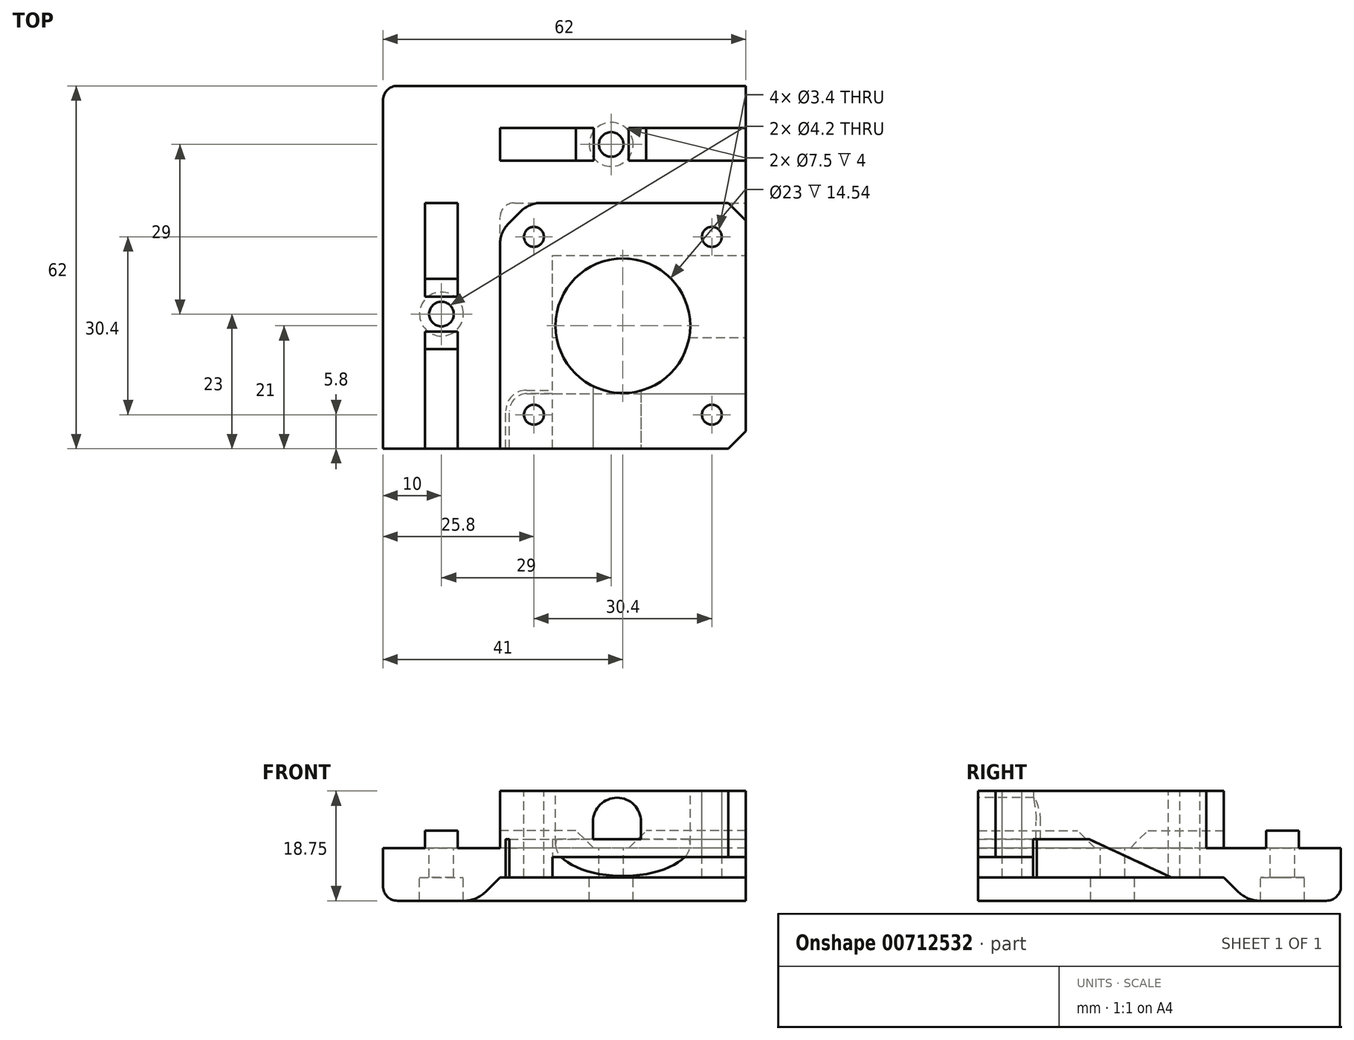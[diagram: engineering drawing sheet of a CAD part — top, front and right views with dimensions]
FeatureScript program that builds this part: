
annotation { "Feature Type Name" : "Feature", "Feature Type Description" : "" }
export const myFeature = defineFeature(function(context is Context, id is Id, definition is map)
    precondition{}
    {
        {
            var Q0;
            Q0=qCreatedBy(makeId("Top.planeOp"),FACE);
            var sketch = newSketch(context, id + "F0", { "sketchPlane" : qUnion([Q0])});
            skLineSegment(sketch, "E0.bottom", {"start": v(0, 0) * mm, "end": v(59, 0) * mm});
            skLineSegment(sketch, "E0.top", {"start": v(0, 54) * mm, "end": v(59, 54) * mm});
            skLineSegment(sketch, "E0.left", {"start": v(0, 0) * mm, "end": v(0, 54) * mm});
            skLineSegment(sketch, "E0.right", {"start": v(59, 0) * mm, "end": v(59, 54) * mm});
            skSolve(sketch);
        }
        {
            var Q0;
            Q0=makeQuery(id+"F0.imprint","IMPRINT",FACE,{"disambiguationData":[TD([[makeQuery(id+"F0.imprint","IMPRINT",EDGE,{"derivedFrom":sQuery(id+"F0.wireOp",EDGE,"E0.bottom")}),1.0]])]});
            extrude(context, id + "F1", {"entities" : qUnion([Q0]), "depth" : 5 * mm, "offsetDistance" : 25 * mm});
        }
        {
            var Q0;
            Q0=makeQuery(id+"F1.opExtrude","CAP_FACE",FACE,{"disambiguationData":[OSD([sQuery(id+"F0.wireOp",EDGE,"E0.bottom"),sQuery(id+"F0.wireOp",EDGE,"E0.top"),sQuery(id+"F0.wireOp",EDGE,"E0.left"),sQuery(id+"F0.wireOp",EDGE,"E0.right")])],"isStart":false});
            var sketch = newSketch(context, id + "F2", { "sketchPlane" : qUnion([Q0])});
            skLineSegment(sketch, "E1.bottom", {"start": v(59, 0) * mm, "end": v(17, 0) * mm});
            skLineSegment(sketch, "E1.top", {"start": v(59, 42) * mm, "end": v(17, 42) * mm});
            skLineSegment(sketch, "E1.left", {"start": v(59, 0) * mm, "end": v(59, 42) * mm});
            skLineSegment(sketch, "E1.right", {"start": v(17, 0) * mm, "end": v(17, 42) * mm});
            skSolve(sketch);
        }
        {
            var Q0;
            Q0=makeQuery(id+"F2.imprint","IMPRINT",FACE,{"disambiguationData":[TD([[makeQuery(id+"F2.imprint","IMPRINT",EDGE,{"derivedFrom":sQuery(id+"F2.wireOp",EDGE,"E1.bottom")}),1.0]])]});
            extrude(context, id + "F3", {"entities" : qUnion([Q0]), "operationType" : NewBodyOperationType.ADD, "depth" : 9.75 * mm, "offsetDistance" : 25 * mm});
        }
        {
            var Q0;
            Q0=makeQuery(id+"F3.boolean.opBoolean","MERGE",FACE,{"derivedFrom":[makeQuery(id+"F1.opExtrude","SWEPT_FACE",FACE,{"disambiguationData":[OSD([sQuery(id+"F0.wireOp",EDGE,"E0.right")])]}),makeQuery(id+"F3.opExtrude","SWEPT_FACE",FACE,{"disambiguationData":[OSD([sQuery(id+"F2.wireOp",EDGE,"E1.left")])]})]});
            var sketch = newSketch(context, id + "F4", { "sketchPlane" : qUnion([Q0])});
            skLineSegment(sketch, "E2", {"start": v(0, 0) * mm, "end": v(0, 6.5) * mm});
            skLineSegment(sketch, "E3", {"start": v(0, 6.5) * mm, "end": v(19, 6.5) * mm});
            skLineSegment(sketch, "E4", {"start": v(19, 6.5) * mm, "end": v(33, 0) * mm});
            skLineSegment(sketch, "E5", {"start": v(33, 0) * mm, "end": v(0, 0) * mm});
            skSolve(sketch);
        }
        {
            var Q0;
            Q0=makeQuery(id+"F4.imprint","IMPRINT",FACE,{"disambiguationData":[TD([[makeQuery(id+"F4.imprint","IMPRINT",EDGE,{"derivedFrom":sQuery(id+"F4.wireOp",EDGE,"E2")}),1.0]])]});
            extrude(context, id + "F5", {"entities" : qUnion([Q0]), "operationType" : NewBodyOperationType.REMOVE, "oppositeDirection" : true, "depth" : 33 * mm, "offsetDistance" : 25 * mm});
        }
        {
            var Q0;
            Q0=makeQuery(id+"F3.opExtrude","CAP_FACE",FACE,{"disambiguationData":[OSD([sQuery(id+"F2.wireOp",EDGE,"E1.bottom"),sQuery(id+"F2.wireOp",EDGE,"E1.top"),sQuery(id+"F2.wireOp",EDGE,"E1.left"),sQuery(id+"F2.wireOp",EDGE,"E1.right")])],"isStart":false});
            var sketch = newSketch(context, id + "F6", { "sketchPlane" : qUnion([Q0])});
            skCircle(sketch, "E6", {"center": v(38, 21) * mm, "radius": 11.5 * mm});
            skCircle(sketch, "E7", {"center": v(22.8, 36.2) * mm, "radius": 1.7 * mm});
            skCircle(sketch, "E8", {"center": v(53.2, 36.2) * mm, "radius": 1.7 * mm});
            skCircle(sketch, "E9", {"center": v(22.8, 5.8) * mm, "radius": 1.7 * mm});
            skCircle(sketch, "E10", {"center": v(53.2, 5.8) * mm, "radius": 1.7 * mm});
            skSolve(sketch);
        }
        {
            var Q0;
            Q0=makeQuery(id+"F6.imprint","IMPRINT",FACE,{"disambiguationData":[TD([[makeQuery(id+"F6.imprint","IMPRINT",EDGE,{"derivedFrom":sQuery(id+"F6.wireOp",EDGE,"E7")}),1.0]])]});
            var Q1;
            Q1=makeQuery(id+"F6.imprint","IMPRINT",FACE,{"disambiguationData":[TD([[makeQuery(id+"F6.imprint","IMPRINT",EDGE,{"derivedFrom":sQuery(id+"F6.wireOp",EDGE,"E6")}),1.0]])]});
            var Q2;
            Q2=makeQuery(id+"F6.imprint","IMPRINT",FACE,{"disambiguationData":[TD([[makeQuery(id+"F6.imprint","IMPRINT",EDGE,{"derivedFrom":sQuery(id+"F6.wireOp",EDGE,"E8")}),1.0]])]});
            var Q3;
            Q3=makeQuery(id+"F6.imprint","IMPRINT",FACE,{"disambiguationData":[TD([[makeQuery(id+"F6.imprint","IMPRINT",EDGE,{"derivedFrom":sQuery(id+"F6.wireOp",EDGE,"E9")}),1.0]])]});
            var Q4;
            Q4=makeQuery(id+"F6.imprint","IMPRINT",FACE,{"disambiguationData":[TD([[makeQuery(id+"F6.imprint","IMPRINT",EDGE,{"derivedFrom":sQuery(id+"F6.wireOp",EDGE,"E10")}),1.0]])]});
            var Q5;
            Q5=makeQuery(id+"F6.imprint","IMPRINT",FACE,{"disambiguationData":[TD([[makeQuery(id+"F6.imprint","IMPRINT",EDGE,{"derivedFrom":sQuery(id+"F6.wireOp",EDGE,"STXgVHVY-l6Oo-r3We-HZuw-ze8qtC1o8g8W")}),1.0]])]});
            extrude(context, id + "F7", {"entities" : qUnion([Q0, Q1, Q2, Q3, Q4, Q5]), "operationType" : NewBodyOperationType.REMOVE, "endBound" : BoundingType.THROUGH_ALL, "oppositeDirection" : true, "depth" : 25 * mm, "offsetDistance" : 25 * mm});
        }
        {
            var Q0;
            Q0=makeQuery(id+"F3.opExtrude","SWEPT_EDGE",EDGE,{"disambiguationData":[OSD([sQuery(id+"F0.wireOp",EDGE,"E0.right"),sQuery(id+"F2.wireOp",EDGE,"E1.top"),sQuery(id+"F2.wireOp",EDGE,"E1.left")])]});
            var Q1;
            Q1=makeQuery(id+"F3.boolean.opBoolean","MERGE",EDGE,{"derivedFrom":[makeQuery(id+"F1.opExtrude","SWEPT_EDGE",EDGE,{"disambiguationData":[OSD([sQuery(id+"F0.wireOp",EDGE,"E0.bottom"),sQuery(id+"F0.wireOp",EDGE,"E0.right")])]}),makeQuery(id+"F3.opExtrude","SWEPT_EDGE",EDGE,{"disambiguationData":[OSD([sQuery(id+"F2.wireOp",EDGE,"E1.bottom"),sQuery(id+"F2.wireOp",EDGE,"E1.left")])]})]});
            chamfer(context, id + "F8", {"entities" : qUnion([Q0, Q1]), "width" : 3 * mm, "tangentPropagation" : true});
        }
        {
            var Q0;
            Q0=makeQuery(id+"F3.boolean.opBoolean","MERGE",FACE,{"derivedFrom":[makeQuery(id+"F7aVUtGTQ7vZGl7_1.boolean.opBoolean","MERGE",FACE,{"derivedFrom":[makeQuery(id+"F1.opExtrude","SWEPT_FACE",FACE,{"disambiguationData":[OSD([sQuery(id+"F0.wireOp",EDGE,"E0.bottom")])]}),makeQuery(id+"F7aVUtGTQ7vZGl7_1.opExtrude","SWEPT_FACE",FACE,{"disambiguationData":[OSD([sQuery(id+"Fs2P3l27It3FXby_1.wireOp",EDGE,"bHcCaI8n-BMMI-Yc99-4eW4-bQ5ukSnPJtkv.top")])]})]}),makeQuery(id+"F3.opExtrude","SWEPT_FACE",FACE,{"disambiguationData":[OSD([sQuery(id+"F2.wireOp",EDGE,"E1.bottom")])]})]});
            var sketch = newSketch(context, id + "F9", { "sketchPlane" : qUnion([Q0])});
            skLineSegment(sketch, "E11.top", {"start": v(32.9, 6.5) * mm, "end": v(41.1, 6.5) * mm});
            skLineSegment(sketch, "E11.left", {"start": v(32.9, 9.5) * mm, "end": v(32.9, 6.5) * mm});
            skLineSegment(sketch, "E11.right", {"start": v(41.1, 9.5) * mm, "end": v(41.1, 6.5) * mm});
            skArc(sketch, "E12.trimOffspring", {"start": v(41.1, 9.5) * mm, "mid": v(37, 13.6) * mm, "end": v(32.9, 9.5) * mm});
            skSolve(sketch);
        }
        {
            var Q0;
            Q0=makeQuery(id+"F9.imprint","IMPRINT",FACE,{"disambiguationData":[TD([[makeQuery(id+"F9.imprint","IMPRINT",EDGE,{"derivedFrom":sQuery(id+"F9.wireOp",EDGE,"E11.top")}),1.0]])]});
            extrude(context, id + "F10", {"entities" : qUnion([Q0]), "operationType" : NewBodyOperationType.REMOVE, "endBound" : BoundingType.UP_TO_NEXT, "oppositeDirection" : true, "depth" : 25 * mm, "offsetDistance" : 25 * mm});
        }
        {
            var Q0;
            Q0=makeQuery(id+"F1.opExtrude","CAP_FACE",FACE,{"disambiguationData":[OSD([sQuery(id+"F0.wireOp",EDGE,"E0.bottom"),sQuery(id+"F0.wireOp",EDGE,"E0.top"),sQuery(id+"F0.wireOp",EDGE,"E0.left"),sQuery(id+"F0.wireOp",EDGE,"E0.right")])],"isStart":false});
            var sketch = newSketch(context, id + "F11", { "sketchPlane" : qUnion([Q0])});
            skLineSegment(sketch, "E13", {"start": v(56, 42) * mm, "end": v(59, 42) * mm});
            skSolve(sketch);
        }
        {
            var Q0;
            {var subQ1=sQuery(id+"F11.wireOp",EDGE,"E13");Q0=makeQuery(id+"F11.imprint","IMPRINT",FACE,{"disambiguationData":[TD([[makeQuery(id+"F11.imprint","IMPRINT",EDGE,{"derivedFrom":subQ1}),1.0]])]});}
            extrude(context, id + "F12", {"entities" : qUnion([Q0]), "operationType" : NewBodyOperationType.REMOVE, "endBound" : BoundingType.THROUGH_ALL, "oppositeDirection" : true, "depth" : 25 * mm, "offsetDistance" : 25 * mm});
        }
        {
            var Q0;
            {var subQ0=sQuery(id+"F2.wireOp",EDGE,"E1.top");Q0=makeQuery(id+"F12.boolean.opBoolean","MERGE",FACE,{"derivedFrom":[makeQuery(id+"F3.opExtrude","SWEPT_FACE",FACE,{"disambiguationData":[OSD([subQ0])]})],"fromTools":[makeQuery(id+"F12.opExtrude","SWEPT_FACE",FACE,{"disambiguationData":[OSD([subQ0,sQuery(id+"F11.wireOp",EDGE,"E13")])]})]});}
            var sketch = newSketch(context, id + "F13", { "sketchPlane" : qUnion([Q0])});
            skLineSegment(sketch, "E14.bottom", {"start": v(-59, 5) * mm, "end": v(-17, 5) * mm});
            skLineSegment(sketch, "E14.top", {"start": v(-59, 0) * mm, "end": v(-17, 0) * mm});
            skLineSegment(sketch, "E14.left", {"start": v(-59, 5) * mm, "end": v(-59, 0) * mm});
            skLineSegment(sketch, "E14.right", {"start": v(-17, 5) * mm, "end": v(-17, 0) * mm});
            skSolve(sketch);
        }
        {
            var Q0;
            Q0=makeQuery(id+"F13.imprint","IMPRINT",FACE,{"disambiguationData":[TD([[makeQuery(id+"F13.imprint","IMPRINT",EDGE,{"derivedFrom":sQuery(id+"F13.wireOp",EDGE,"E14.top")}),1.0]])]});
            extrude(context, id + "F14", {"entities" : qUnion([Q0]), "operationType" : NewBodyOperationType.ADD, "depth" : 20 * mm, "offsetDistance" : 25 * mm});
        }
        {
            var Q0;
            {var subQ0=sQuery(id+"F2.wireOp",EDGE,"E1.right");Q0=makeQuery(id+"F14.boolean.opBoolean","MERGE",FACE,{"derivedFrom":[makeQuery(id+"F12.boolean.opBoolean","MERGE",FACE,{"derivedFrom":[makeQuery(id+"F3.opExtrude","SWEPT_FACE",FACE,{"disambiguationData":[OSD([subQ0])]})],"fromTools":[makeQuery(id+"F12.opExtrude","SWEPT_FACE",FACE,{"disambiguationData":[OSD([subQ0])]})]}),makeQuery(id+"F14.opExtrude","SWEPT_FACE",FACE,{"disambiguationData":[OSD([sQuery(id+"F13.wireOp",EDGE,"E14.right")])]})]});}
            var sketch = newSketch(context, id + "F15", { "sketchPlane" : qUnion([Q0])});
            skLineSegment(sketch, "E15.bottom", {"start": v(-62, 5) * mm, "end": v(0, 5) * mm});
            skLineSegment(sketch, "E15.top", {"start": v(-62, 0) * mm, "end": v(0, 0) * mm});
            skLineSegment(sketch, "E15.left", {"start": v(-62, 5) * mm, "end": v(-62, 0) * mm});
            skLineSegment(sketch, "E15.right", {"start": v(0, 5) * mm, "end": v(0, 0) * mm});
            skSolve(sketch);
        }
        {
            var Q0;
            Q0=makeQuery(id+"F15.imprint","IMPRINT",FACE,{"disambiguationData":[TD([[makeQuery(id+"F15.imprint","IMPRINT",EDGE,{"derivedFrom":sQuery(id+"F15.wireOp",EDGE,"E15.top")}),-1.0]])]});
            extrude(context, id + "F16", {"entities" : qUnion([Q0]), "operationType" : NewBodyOperationType.ADD, "depth" : 20 * mm, "offsetDistance" : 25 * mm});
        }
        {
            var Q0;
            Q0=makeQuery(id+"F16.boolean.opBoolean","MERGE",FACE,{"derivedFrom":[makeQuery(id+"F14.boolean.opBoolean","MERGE",FACE,{"derivedFrom":[makeQuery(id+"F1.opExtrude","CAP_FACE",FACE,{"disambiguationData":[OSD([sQuery(id+"F0.wireOp",EDGE,"E0.bottom"),sQuery(id+"F0.wireOp",EDGE,"E0.top"),sQuery(id+"F0.wireOp",EDGE,"E0.left"),sQuery(id+"F0.wireOp",EDGE,"E0.right")])],"isStart":false}),makeQuery(id+"F14.opExtrude","SWEPT_FACE",FACE,{"disambiguationData":[OSD([sQuery(id+"F13.wireOp",EDGE,"E14.bottom")])]})]}),makeQuery(id+"F16.opExtrude","SWEPT_FACE",FACE,{"disambiguationData":[OSD([sQuery(id+"F15.wireOp",EDGE,"E15.bottom")])]})]});
            var sketch = newSketch(context, id + "F17", { "sketchPlane" : qUnion([Q0])});
            skLineSegment(sketch, "E16.bottom", {"start": v(59, 54.8) * mm, "end": v(17, 54.8) * mm});
            skLineSegment(sketch, "E16.top", {"start": v(59, 49.2) * mm, "end": v(17, 49.2) * mm});
            skLineSegment(sketch, "E16.left", {"start": v(59, 54.8) * mm, "end": v(59, 49.2) * mm});
            skLineSegment(sketch, "E16.right", {"start": v(17, 54.8) * mm, "end": v(17, 49.2) * mm});
            skLineSegment(sketch, "E17.bottom", {"start": v(4.2, 0) * mm, "end": v(9.8, 0) * mm});
            skLineSegment(sketch, "E17.top", {"start": v(4.2, 42) * mm, "end": v(9.8, 42) * mm});
            skLineSegment(sketch, "E17.left", {"start": v(4.2, 0) * mm, "end": v(4.2, 42) * mm});
            skLineSegment(sketch, "E17.right", {"start": v(9.8, 0) * mm, "end": v(9.8, 42) * mm});
            skLineSegment(sketch, "E18.bottom", {"start": v(22, 54.8) * mm, "end": v(28, 54.8) * mm});
            skLineSegment(sketch, "E19.bottom", {"start": v(33, 54.8) * mm, "end": v(39, 54.8) * mm});
            skLineSegment(sketch, "E19.top", {"start": v(33, 49.2) * mm, "end": v(39, 49.2) * mm});
            skLineSegment(sketch, "E19.left", {"start": v(33, 54.8) * mm, "end": v(33, 49.2) * mm});
            skLineSegment(sketch, "E19.right", {"start": v(39, 54.8) * mm, "end": v(39, 49.2) * mm});
            skLineSegment(sketch, "E20.left", {"start": v(4.2, 37) * mm, "end": v(4.2, 31) * mm});
            skLineSegment(sketch, "E20.right", {"start": v(9.8, 37) * mm, "end": v(9.8, 31) * mm});
            skLineSegment(sketch, "E21.bottom", {"start": v(4.2, 26) * mm, "end": v(9.8, 26) * mm});
            skLineSegment(sketch, "E21.top", {"start": v(4.2, 20) * mm, "end": v(9.8, 20) * mm});
            skLineSegment(sketch, "E21.left", {"start": v(4.2, 26) * mm, "end": v(4.2, 20) * mm});
            skLineSegment(sketch, "E21.right", {"start": v(9.8, 26) * mm, "end": v(9.8, 20) * mm});
            skSolve(sketch);
        }
        {
            var Q0;
            {var subQ0=sQuery(id+"F17.wireOp",EDGE,"E20.top");Q0=makeQuery(id+"F17.imprint","IMPRINT",FACE,{"disambiguationData":[TD([[makeQuery(id+"F17.imprint","IMPRINT",EDGE,{"derivedFrom":subQ0}),-1.0]])]});}
            var Q1;
            {var subQ0=sQuery(id+"F17.wireOp",EDGE,"E17.top");Q1=makeQuery(id+"F17.imprint","IMPRINT",FACE,{"disambiguationData":[TD([[makeQuery(id+"F17.imprint","IMPRINT",EDGE,{"derivedFrom":subQ0}),-1.0]])]});}
            var Q2;
            {var subQ0=sQuery(id+"F17.wireOp",EDGE,"E17.bottom");Q2=makeQuery(id+"F17.imprint","IMPRINT",FACE,{"disambiguationData":[TD([[makeQuery(id+"F17.imprint","IMPRINT",EDGE,{"derivedFrom":subQ0}),1.0]])]});}
            var Q3;
            {var subQ0=sQuery(id+"F17.wireOp",EDGE,"E16.right");Q3=makeQuery(id+"F17.imprint","IMPRINT",FACE,{"disambiguationData":[TD([[makeQuery(id+"F17.imprint","IMPRINT",EDGE,{"derivedFrom":subQ0}),1.0]])]});}
            var Q4;
            {var subQ0=sQuery(id+"F17.wireOp",EDGE,"E18.right");Q4=makeQuery(id+"F17.imprint","IMPRINT",FACE,{"disambiguationData":[TD([[makeQuery(id+"F17.imprint","IMPRINT",EDGE,{"derivedFrom":subQ0}),1.0]])]});}
            var Q5;
            {var subQ0=sQuery(id+"F17.wireOp",EDGE,"E16.left");Q5=makeQuery(id+"F17.imprint","IMPRINT",FACE,{"disambiguationData":[TD([[makeQuery(id+"F17.imprint","IMPRINT",EDGE,{"derivedFrom":subQ0}),1.0]])]});}
            extrude(context, id + "F18", {"entities" : qUnion([Q0, Q1, Q2, Q3, Q4, Q5]), "operationType" : NewBodyOperationType.ADD, "depth" : 3 * mm, "offsetDistance" : 25 * mm});
        }
        {
            var Q0;
            Q0=makeQuery(id+"F18.opExtrude","CAP_EDGE",EDGE,{"disambiguationData":[OSD([sQuery(id+"F17.wireOp",EDGE,"E19.right")])],"isStart":false});
            var Q1;
            Q1=makeQuery(id+"F18.opExtrude","CAP_EDGE",EDGE,{"disambiguationData":[OSD([sQuery(id+"F17.wireOp",EDGE,"E19.left")])],"isStart":false});
            var Q2;
            Q2=makeQuery(id+"F18.opExtrude","CAP_EDGE",EDGE,{"disambiguationData":[OSD([sQuery(id+"F17.wireOp",EDGE,"E18.right")])],"isStart":false});
            var Q3;
            Q3=makeQuery(id+"F18.opExtrude","CAP_EDGE",EDGE,{"disambiguationData":[OSD([sQuery(id+"F17.wireOp",EDGE,"E18.left")])],"isStart":false});
            var Q4;
            Q4=makeQuery(id+"F18.opExtrude","CAP_EDGE",EDGE,{"disambiguationData":[OSD([sQuery(id+"F17.wireOp",EDGE,"E20.bottom")])],"isStart":false});
            var Q5;
            Q5=makeQuery(id+"F18.opExtrude","CAP_EDGE",EDGE,{"disambiguationData":[OSD([sQuery(id+"F17.wireOp",EDGE,"E20.top")])],"isStart":false});
            var Q6;
            Q6=makeQuery(id+"F18.opExtrude","CAP_EDGE",EDGE,{"disambiguationData":[OSD([sQuery(id+"F17.wireOp",EDGE,"E21.bottom")])],"isStart":false});
            var Q7;
            Q7=makeQuery(id+"F18.opExtrude","CAP_EDGE",EDGE,{"disambiguationData":[OSD([sQuery(id+"F17.wireOp",EDGE,"E21.top")])],"isStart":false});
            chamfer(context, id + "F19", {"entities" : qUnion([Q0, Q1, Q2, Q3, Q4, Q5, Q6, Q7]), "width" : 3 * mm, "tangentPropagation" : true});
        }
        {
            var Q0;
            Q0=makeQuery(id+"F16.boolean.opBoolean","MERGE",FACE,{"derivedFrom":[makeQuery(id+"F14.boolean.opBoolean","MERGE",FACE,{"derivedFrom":[makeQuery(id+"F1.opExtrude","CAP_FACE",FACE,{"disambiguationData":[OSD([sQuery(id+"F0.wireOp",EDGE,"E0.bottom"),sQuery(id+"F0.wireOp",EDGE,"E0.top"),sQuery(id+"F0.wireOp",EDGE,"E0.left"),sQuery(id+"F0.wireOp",EDGE,"E0.right")])],"isStart":false}),makeQuery(id+"F14.opExtrude","SWEPT_FACE",FACE,{"disambiguationData":[OSD([sQuery(id+"F13.wireOp",EDGE,"E14.bottom")])]})]}),makeQuery(id+"F16.opExtrude","SWEPT_FACE",FACE,{"disambiguationData":[OSD([sQuery(id+"F15.wireOp",EDGE,"E15.bottom")])]})]});
            var sketch = newSketch(context, id + "F20", { "sketchPlane" : qUnion([Q0])});
            skCircle(sketch, "E22", {"center": v(36, 52) * mm, "radius": 2.1 * mm});
            skCircle(sketch, "E23", {"center": v(7, 23) * mm, "radius": 2.1 * mm});
            skPoint(sketch, "E23.centerSnap0", {"position": v(7, 20) * mm});
            skSolve(sketch);
        }
        {
            var Q0;
            Q0=makeQuery(id+"F20.imprint","IMPRINT",FACE,{"disambiguationData":[TD([[makeQuery(id+"F20.imprint","IMPRINT",EDGE,{"derivedFrom":sQuery(id+"F20.wireOp",EDGE,"3zCe3JNz-EdKe-6DJv-AUvG-g2xwXIvxGB8e")}),1.0]])]});
            var Q1;
            Q1=makeQuery(id+"F20.imprint","IMPRINT",FACE,{"disambiguationData":[TD([[makeQuery(id+"F20.imprint","IMPRINT",EDGE,{"derivedFrom":sQuery(id+"F20.wireOp",EDGE,"E23")}),1.0]])]});
            var Q2;
            Q2=makeQuery(id+"F20.imprint","IMPRINT",FACE,{"disambiguationData":[TD([[makeQuery(id+"F20.imprint","IMPRINT",EDGE,{"derivedFrom":sQuery(id+"F20.wireOp",EDGE,"QEAMcVXS-o3zG-8i1c-1XAg-jgGJsIAo5R6x")}),1.0]])]});
            var Q3;
            Q3=makeQuery(id+"F20.imprint","IMPRINT",FACE,{"disambiguationData":[TD([[makeQuery(id+"F20.imprint","IMPRINT",EDGE,{"derivedFrom":sQuery(id+"F20.wireOp",EDGE,"E22")}),1.0]])]});
            extrude(context, id + "F21", {"entities" : qUnion([Q0, Q1, Q2, Q3]), "operationType" : NewBodyOperationType.REMOVE, "endBound" : BoundingType.THROUGH_ALL, "oppositeDirection" : true, "depth" : 25 * mm, "offsetDistance" : 25 * mm});
        }
        {
            var Q0;
            Q0=makeQuery(id+"F16.boolean.opBoolean","MERGE",FACE,{"derivedFrom":[makeQuery(id+"F14.boolean.opBoolean","MERGE",FACE,{"derivedFrom":[makeQuery(id+"F1.opExtrude","CAP_FACE",FACE,{"disambiguationData":[OSD([sQuery(id+"F0.wireOp",EDGE,"E0.bottom"),sQuery(id+"F0.wireOp",EDGE,"E0.top"),sQuery(id+"F0.wireOp",EDGE,"E0.left"),sQuery(id+"F0.wireOp",EDGE,"E0.right")])],"isStart":true}),makeQuery(id+"F14.opExtrude","SWEPT_FACE",FACE,{"disambiguationData":[OSD([sQuery(id+"F13.wireOp",EDGE,"E14.top")])]})]}),makeQuery(id+"F16.opExtrude","SWEPT_FACE",FACE,{"disambiguationData":[OSD([sQuery(id+"F15.wireOp",EDGE,"E15.top")])]})]});
            var sketch = newSketch(context, id + "F22", { "sketchPlane" : qUnion([Q0])});
            skLineSegment(sketch, "E24", {"start": v(17, 0) * mm, "end": v(17, -42) * mm});
            skLineSegment(sketch, "E25", {"start": v(17, -42) * mm, "end": v(59, -42) * mm});
            skCircle(sketch, "E26", {"center": v(36, -52) * mm, "radius": 3.75 * mm});
            skCircle(sketch, "E27", {"center": v(7, -23) * mm, "radius": 3.75 * mm});
            skSolve(sketch);
        }
        {
            var Q0;
            {var subQ4=sQuery(id+"F22.wireOp",EDGE,"E24");Q0=makeQuery(id+"F22.imprint","IMPRINT",FACE,{"disambiguationData":[TD([[makeQuery(id+"F22.imprint","IMPRINT",EDGE,{"derivedFrom":subQ4}),-1.0]])]});}
            extrude(context, id + "F23", {"entities" : qUnion([Q0]), "operationType" : NewBodyOperationType.ADD, "depth" : 4 * mm, "offsetDistance" : 25 * mm});
        }
        {
            var Q0;
            Q0=makeQuery(id+"F23.opExtrude","SWEPT_EDGE",EDGE,{"disambiguationData":[OSD([sQuery(id+"F22.wireOp",EDGE,"E24"),sQuery(id+"F22.wireOp",EDGE,"E25")])]});
            var Q1;
            Q1=makeQuery(id+"F23.opExtrude","CAP_EDGE",EDGE,{"disambiguationData":[OSD([sQuery(id+"F15.wireOp",EDGE,"E15.top")])],"isStart":false});
            var Q2;
            {var subQ0=sQuery(id+"F15.wireOp",EDGE,"E15.left");Q2=makeQuery(id+"F23.boolean.opBoolean","MERGE",EDGE,{"derivedFrom":[makeQuery(id+"F16.opExtrude","CAP_EDGE",EDGE,{"disambiguationData":[OSD([subQ0])],"isStart":false}),makeQuery(id+"F23.opExtrude","SWEPT_EDGE",EDGE,{"disambiguationData":[OSD([sQuery(id+"F13.wireOp",EDGE,"E14.top"),sQuery(id+"F15.wireOp",EDGE,"E15.top"),subQ0])]})]});}
            var Q3;
            Q3=makeQuery(id+"F23.opExtrude","CAP_EDGE",EDGE,{"disambiguationData":[OSD([sQuery(id+"F13.wireOp",EDGE,"E14.top"),sQuery(id+"F15.wireOp",EDGE,"E15.top"),sQuery(id+"F15.wireOp",EDGE,"E15.left")])],"isStart":false});
            fillet(context, id + "F24", {"entities" : qUnion([Q0, Q1, Q2, Q3]), "tangentPropagation" : true, "radius" : 2.5 * mm, "defaultsChanged" : false, "vertexSettings" : [], "allowEdgeOverflow" : false});
        }
        {
            var Q0;
            Q0=makeQuery(id+"F23.opExtrude","CAP_EDGE",EDGE,{"disambiguationData":[OSD([sQuery(id+"F22.wireOp",EDGE,"E25")])],"isStart":false});
            chamfer(context, id + "F25", {"entities" : qUnion([Q0]), "width" : 4 * mm, "tangentPropagation" : true});
        }
        {
            var Q0;
            {var subQ0=sQuery(id+"F22.wireOp",EDGE,"E25");Q0=makeQuery(id+"F25.opChamfer","BLEND_EDGE",EDGE,{"blendedFrom":[makeQuery(id+"F23.opExtrude","CAP_EDGE",EDGE,{"disambiguationData":[OSD([subQ0])],"isStart":false}),makeQuery(id+"F23.opExtrude","CAP_FACE",FACE,{"disambiguationData":[OSD([sQuery(id+"F0.wireOp",EDGE,"E0.bottom"),sQuery(id+"F0.wireOp",EDGE,"E0.right"),sQuery(id+"F13.wireOp",EDGE,"E14.top"),sQuery(id+"F13.wireOp",EDGE,"E14.left"),sQuery(id+"F15.wireOp",EDGE,"E15.top"),sQuery(id+"F15.wireOp",EDGE,"E15.left"),sQuery(id+"F15.wireOp",EDGE,"E15.right"),sQuery(id+"F22.wireOp",EDGE,"E24"),subQ0,sQuery(id+"F22.wireOp",EDGE,"E26"),sQuery(id+"F22.wireOp",EDGE,"E27")])],"isStart":false})],"blendedInto":[makeQuery(id+"F23.opExtrude","CAP_FACE",FACE,{"disambiguationData":[OSD([sQuery(id+"F0.wireOp",EDGE,"E0.bottom"),sQuery(id+"F0.wireOp",EDGE,"E0.right"),sQuery(id+"F13.wireOp",EDGE,"E14.top"),sQuery(id+"F13.wireOp",EDGE,"E14.left"),sQuery(id+"F15.wireOp",EDGE,"E15.top"),sQuery(id+"F15.wireOp",EDGE,"E15.left"),sQuery(id+"F15.wireOp",EDGE,"E15.right"),sQuery(id+"F22.wireOp",EDGE,"E24"),subQ0,sQuery(id+"F22.wireOp",EDGE,"E26"),sQuery(id+"F22.wireOp",EDGE,"E27")])],"isStart":false})]});}
            fillet(context, id + "F26", {"entities" : qUnion([Q0]), "tangentPropagation" : true, "radius" : 5 * mm, "defaultsChanged" : false, "vertexSettings" : [], "allowEdgeOverflow" : false});
        }
        {
            var Q0;
            Q0=makeQuery(id+"F5.boolean.opBoolean","COPY",FACE,{"derivedFrom":makeQuery(id+"F5.opExtrude","CAP_FACE",FACE,{"disambiguationData":[OSD([sQuery(id+"F4.wireOp",EDGE,"E2"),sQuery(id+"F4.wireOp",EDGE,"E3"),sQuery(id+"F4.wireOp",EDGE,"E4"),sQuery(id+"F4.wireOp",EDGE,"E5")])],"isStart":false})});
            var sketch = newSketch(context, id + "F27", { "sketchPlane" : qUnion([Q0])});
            skLineSegment(sketch, "E28.bottom", {"start": v(0, 0) * mm, "end": v(10, 0) * mm});
            skLineSegment(sketch, "E28.top", {"start": v(0, 6.5) * mm, "end": v(10, 6.5) * mm});
            skLineSegment(sketch, "E28.left", {"start": v(0, 0) * mm, "end": v(0, 6.5) * mm});
            skLineSegment(sketch, "E28.right", {"start": v(10, 0) * mm, "end": v(10, 6.5) * mm});
            skSolve(sketch);
        }
        {
            var Q0;
            Q0=makeQuery(id+"F27.imprint","IMPRINT",FACE,{"disambiguationData":[TD([[makeQuery(id+"F27.imprint","IMPRINT",EDGE,{"derivedFrom":sQuery(id+"F27.wireOp",EDGE,"E28.bottom")}),1.0]])]});
            extrude(context, id + "F28", {"entities" : qUnion([Q0]), "operationType" : NewBodyOperationType.REMOVE, "oppositeDirection" : true, "depth" : 8 * mm, "offsetDistance" : 25 * mm});
        }
        {
            var Q0;
            {var subQ1=sQuery(id+"F4.wireOp",EDGE,"E3");Q0=makeQuery(id+"F28.boolean.opBoolean","MERGE",FACE,{"derivedFrom":[makeQuery(id+"F10.boolean.opBoolean","SPLIT",FACE,{"disambiguationData":[TD([makeQuery(id+"F10.opExtrude","SWEPT_FACE",FACE,{"disambiguationData":[OSD([sQuery(id+"F9.wireOp",EDGE,"E11.left")])]})])],"derivedFrom":makeQuery(id+"F5.boolean.opBoolean","COPY",FACE,{"derivedFrom":makeQuery(id+"F5.opExtrude","SWEPT_FACE",FACE,{"disambiguationData":[OSD([subQ1])]})})})],"fromTools":[makeQuery(id+"F28.opExtrude","SWEPT_FACE",FACE,{"disambiguationData":[OSD([sQuery(id+"F27.wireOp",EDGE,"E28.top")])]})]});}
            var sketch = newSketch(context, id + "F29", { "sketchPlane" : qUnion([Q0])});
            skLineSegment(sketch, "E29.bottom", {"start": v(18.6, 0) * mm, "end": v(32.9, 0) * mm});
            skLineSegment(sketch, "E29.top", {"start": v(18.6, -9.4) * mm, "end": v(32.9, -9.4) * mm});
            skLineSegment(sketch, "E29.left", {"start": v(18.6, 0) * mm, "end": v(18.6, -9.4) * mm});
            skLineSegment(sketch, "E29.right", {"start": v(32.9, 0) * mm, "end": v(32.9, -9.4) * mm});
            skSolve(sketch);
        }
        {
            var Q0;
            Q0=makeQuery(id+"F29.imprint","IMPRINT",FACE,{"disambiguationData":[TD([[makeQuery(id+"F29.imprint","IMPRINT",EDGE,{"derivedFrom":sQuery(id+"F29.wireOp",EDGE,"E29.bottom")}),-1.0]])]});
            extrude(context, id + "F30", {"entities" : qUnion([Q0]), "depth" : 3 * mm, "offsetDistance" : 25 * mm});
        }
        {
            var Q0;
            Q0=makeQuery(id+"F30.opExtrude","CAP_FACE",FACE,{"disambiguationData":[OSD([sQuery(id+"F6.wireOp",EDGE,"E9"),sQuery(id+"F27.wireOp",EDGE,"E28.top"),sQuery(id+"F29.wireOp",EDGE,"E29.bottom"),sQuery(id+"F29.wireOp",EDGE,"E29.top"),sQuery(id+"F29.wireOp",EDGE,"E29.left"),sQuery(id+"F29.wireOp",EDGE,"E29.right")])],"isStart":false});
            var sketch = newSketch(context, id + "F31", { "sketchPlane" : qUnion([Q0])});
            skLineSegment(sketch, "E30.bottom", {"start": v(18.6, 0) * mm, "end": v(26, 0) * mm});
            skLineSegment(sketch, "E30.top", {"start": v(18.6, -9.4) * mm, "end": v(26, -9.4) * mm});
            skLineSegment(sketch, "E30.left", {"start": v(18.6, 0) * mm, "end": v(18.6, -9.4) * mm});
            skLineSegment(sketch, "E30.right", {"start": v(26, 0) * mm, "end": v(26, -9.4) * mm});
            skSolve(sketch);
        }
        {
            var Q0;
            Q0=makeQuery(id+"F31.imprint","IMPRINT",FACE,{"disambiguationData":[TD([[makeQuery(id+"F31.imprint","IMPRINT",EDGE,{"derivedFrom":sQuery(id+"F31.wireOp",EDGE,"E30.bottom")}),-1.0]])]});
            var Q1;
            {var subQ1=sQuery(id+"F0.wireOp",EDGE,"E0.bottom");var subQ3=sQuery(id+"F0.wireOp",EDGE,"E0.right");var subQ5=sQuery(id+"F13.wireOp",EDGE,"E14.top");var subQ6=sQuery(id+"F15.wireOp",EDGE,"E15.top");Q1=makeQuery(id+"F23.boolean.opBoolean","SPLIT",FACE,{"disambiguationData":[TD([makeQuery(id+"F1.opExtrude","SWEPT_FACE",FACE,{"disambiguationData":[OSD([subQ1])]})])],"derivedFrom":makeQuery(id+"F16.boolean.opBoolean","MERGE",FACE,{"derivedFrom":[makeQuery(id+"F14.boolean.opBoolean","MERGE",FACE,{"derivedFrom":[makeQuery(id+"F1.opExtrude","CAP_FACE",FACE,{"disambiguationData":[OSD([subQ1,sQuery(id+"F0.wireOp",EDGE,"E0.top"),sQuery(id+"F0.wireOp",EDGE,"E0.left"),subQ3])],"isStart":true}),makeQuery(id+"F14.opExtrude","SWEPT_FACE",FACE,{"disambiguationData":[OSD([subQ5])]})]}),makeQuery(id+"F16.opExtrude","SWEPT_FACE",FACE,{"disambiguationData":[OSD([subQ6])]})]})});}
            extrude(context, id + "F32", {"entities" : qUnion([Q0]), "operationType" : NewBodyOperationType.ADD, "endBound" : BoundingType.UP_TO_SURFACE, "depth" : 25 * mm, "endBoundEntityFace" : qUnion([Q1]), "offsetDistance" : 25 * mm});
        }
        {
            var Q0;
            {var subQ1=sQuery(id+"F0.wireOp",EDGE,"E0.right");Q0=makeQuery(id+"F10.boolean.opBoolean","SPLIT",FACE,{"disambiguationData":[TD([makeQuery(id+"F1.opExtrude","SWEPT_FACE",FACE,{"disambiguationData":[OSD([subQ1])]})])],"derivedFrom":makeQuery(id+"F5.boolean.opBoolean","COPY",FACE,{"derivedFrom":makeQuery(id+"F5.opExtrude","SWEPT_FACE",FACE,{"disambiguationData":[OSD([sQuery(id+"F4.wireOp",EDGE,"E3")])]})})});}
            var sketch = newSketch(context, id + "F33", { "sketchPlane" : qUnion([Q0])});
            skLineSegment(sketch, "E31.bottom", {"start": v(41.1, 0) * mm, "end": v(59, 0) * mm});
            skLineSegment(sketch, "E31.top", {"start": v(41.1, -9.4) * mm, "end": v(59, -9.4) * mm});
            skLineSegment(sketch, "E31.left", {"start": v(41.1, 0) * mm, "end": v(41.1, -9.4) * mm});
            skLineSegment(sketch, "E31.right", {"start": v(59, 0) * mm, "end": v(59, -9.4) * mm});
            skSolve(sketch);
        }
        {
            var Q0;
            {var subQ4=sQuery(id+"F33.wireOp",EDGE,"E31.top");Q0=makeQuery(id+"F33.imprint","IMPRINT",FACE,{"disambiguationData":[TD([[makeQuery(id+"F33.imprint","IMPRINT",EDGE,{"derivedFrom":subQ4}),1.0]])]});}
            extrude(context, id + "F34", {"entities" : qUnion([Q0]), "depth" : 3 * mm, "offsetDistance" : 25 * mm});
        }
        {
            var Q0;
            Q0=makeQuery(id+"F30.opExtrude","SWEPT_FACE",FACE,{"disambiguationData":[OSD([sQuery(id+"F29.wireOp",EDGE,"E29.right")])]});
            var Q1;
            Q1=makeQuery(id+"F34.opExtrude","SWEPT_BODY",BODY,{"disambiguationData":[OSD([sQuery(id+"F0.wireOp",EDGE,"E0.bottom"),sQuery(id+"F0.wireOp",EDGE,"E0.right"),sQuery(id+"F2.wireOp",EDGE,"E1.bottom"),sQuery(id+"F2.wireOp",EDGE,"E1.left"),sQuery(id+"F4.wireOp",EDGE,"E3"),sQuery(id+"F6.wireOp",EDGE,"E10"),sQuery(id+"F33.wireOp",EDGE,"E31.bottom"),sQuery(id+"F33.wireOp",EDGE,"E31.top"),sQuery(id+"F33.wireOp",EDGE,"E31.left"),sQuery(id+"F33.wireOp",EDGE,"E31.right")])]});
            extrude(context, id + "F35", {"entities" : qUnion([Q0]), "operationType" : NewBodyOperationType.ADD, "endBound" : BoundingType.UP_TO_BODY, "depth" : 25 * mm, "endBoundEntityBody" : qUnion([Q1]), "offsetDistance" : 25 * mm});
        }
        {
            var Q0;
            Q0=makeQuery(id+"F32.boolean.opBoolean","MERGE",EDGE,{"derivedFrom":[makeQuery(id+"F30.opExtrude","SWEPT_EDGE",EDGE,{"disambiguationData":[OSD([sQuery(id+"F29.wireOp",EDGE,"E29.top"),sQuery(id+"F29.wireOp",EDGE,"E29.left")])]}),makeQuery(id+"F32.opExtrude","SWEPT_EDGE",EDGE,{"disambiguationData":[OSD([sQuery(id+"F31.wireOp",EDGE,"E30.top"),sQuery(id+"F31.wireOp",EDGE,"E30.left")])]})]});
            fillet(context, id + "F36", {"entities" : qUnion([Q0]), "tangentPropagation" : true, "radius" : 3 * mm, "defaultsChanged" : true, "vertexSettings" : [], "allowEdgeOverflow" : false});
        }
        {
            var Q0;
            Q0=makeQuery(id+"F28.boolean.opBoolean","COPY",EDGE,{"derivedFrom":makeQuery(id+"F28.opExtrude","CAP_EDGE",EDGE,{"disambiguationData":[OSD([sQuery(id+"F27.wireOp",EDGE,"E28.right")])],"isStart":false})});
            fillet(context, id + "F37", {"entities" : qUnion([Q0]), "tangentPropagation" : true, "radius" : 3.5 * mm, "defaultsChanged" : true, "vertexSettings" : [], "allowEdgeOverflow" : false});
        }
        {
            var Q0;
            {var subQ0=sQuery(id+"F2.wireOp",EDGE,"E1.right");var subQ1=sQuery(id+"F2.wireOp",EDGE,"E1.top");Q0=makeQuery(id+"F12.boolean.opBoolean","MERGE",EDGE,{"derivedFrom":[makeQuery(id+"F3.opExtrude","SWEPT_EDGE",EDGE,{"disambiguationData":[OSD([subQ1,subQ0])]})],"fromTools":[makeQuery(id+"F12.opExtrude","SWEPT_EDGE",EDGE,{"disambiguationData":[OSD([subQ1,subQ0])]})]});}
            chamfer(context, id + "F38", {"entities" : qUnion([Q0]), "width" : 5 * mm, "tangentPropagation" : true});
        }
        {
            var Q0;
            {var subQ0=sQuery(id+"F2.wireOp",EDGE,"E1.right");var subQ1=sQuery(id+"F2.wireOp",EDGE,"E1.top");Q0=makeQuery(id+"F38.opChamfer","BLEND_EDGE",EDGE,{"blendedFrom":[makeQuery(id+"F12.boolean.opBoolean","MERGE",EDGE,{"derivedFrom":[makeQuery(id+"F3.opExtrude","SWEPT_EDGE",EDGE,{"disambiguationData":[OSD([subQ1,subQ0])]})],"fromTools":[makeQuery(id+"F12.opExtrude","SWEPT_EDGE",EDGE,{"disambiguationData":[OSD([subQ1,subQ0])]})]}),makeQuery(id+"F14.boolean.opBoolean","MERGE",FACE,{"derivedFrom":[makeQuery(id+"F12.boolean.opBoolean","MERGE",FACE,{"derivedFrom":[makeQuery(id+"F3.opExtrude","SWEPT_FACE",FACE,{"disambiguationData":[OSD([subQ0])]})],"fromTools":[makeQuery(id+"F12.opExtrude","SWEPT_FACE",FACE,{"disambiguationData":[OSD([subQ0])]})]}),makeQuery(id+"F14.opExtrude","SWEPT_FACE",FACE,{"disambiguationData":[OSD([sQuery(id+"F13.wireOp",EDGE,"E14.right")])]})]})],"blendedInto":[makeQuery(id+"F14.boolean.opBoolean","MERGE",FACE,{"derivedFrom":[makeQuery(id+"F12.boolean.opBoolean","MERGE",FACE,{"derivedFrom":[makeQuery(id+"F3.opExtrude","SWEPT_FACE",FACE,{"disambiguationData":[OSD([subQ0])]})],"fromTools":[makeQuery(id+"F12.opExtrude","SWEPT_FACE",FACE,{"disambiguationData":[OSD([subQ0])]})]}),makeQuery(id+"F14.opExtrude","SWEPT_FACE",FACE,{"disambiguationData":[OSD([sQuery(id+"F13.wireOp",EDGE,"E14.right")])]})]})]});}
            var Q1;
            {var subQ0=sQuery(id+"F2.wireOp",EDGE,"E1.top");var subQ1=sQuery(id+"F2.wireOp",EDGE,"E1.right");Q1=makeQuery(id+"F38.opChamfer","BLEND_EDGE",EDGE,{"blendedFrom":[makeQuery(id+"F12.boolean.opBoolean","MERGE",EDGE,{"derivedFrom":[makeQuery(id+"F3.opExtrude","SWEPT_EDGE",EDGE,{"disambiguationData":[OSD([subQ0,subQ1])]})],"fromTools":[makeQuery(id+"F12.opExtrude","SWEPT_EDGE",EDGE,{"disambiguationData":[OSD([subQ0,subQ1])]})]}),makeQuery(id+"F12.boolean.opBoolean","MERGE",FACE,{"derivedFrom":[makeQuery(id+"F3.opExtrude","SWEPT_FACE",FACE,{"disambiguationData":[OSD([subQ0])]})],"fromTools":[makeQuery(id+"F12.opExtrude","SWEPT_FACE",FACE,{"disambiguationData":[OSD([subQ0,sQuery(id+"F11.wireOp",EDGE,"E13")])]})]})],"blendedInto":[makeQuery(id+"F12.boolean.opBoolean","MERGE",FACE,{"derivedFrom":[makeQuery(id+"F3.opExtrude","SWEPT_FACE",FACE,{"disambiguationData":[OSD([subQ0])]})],"fromTools":[makeQuery(id+"F12.opExtrude","SWEPT_FACE",FACE,{"disambiguationData":[OSD([subQ0,sQuery(id+"F11.wireOp",EDGE,"E13")])]})]})]});}
            fillet(context, id + "F39", {"entities" : qUnion([Q0, Q1]), "tangentPropagation" : true, "radius" : 5 * mm, "defaultsChanged" : false, "vertexSettings" : [], "allowEdgeOverflow" : false});
        }
    });
